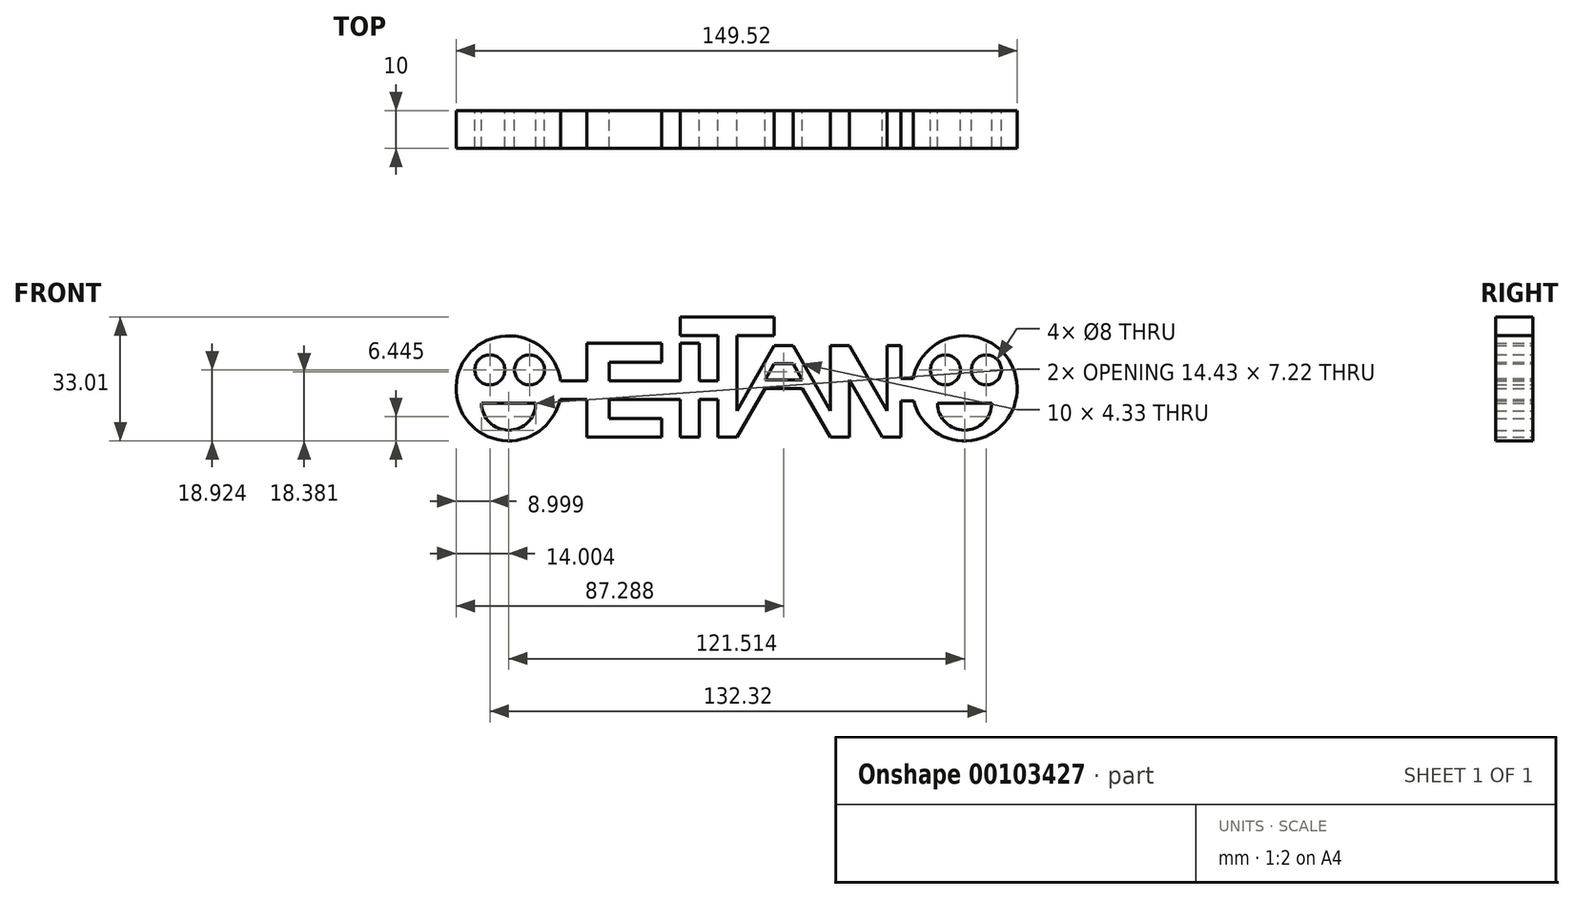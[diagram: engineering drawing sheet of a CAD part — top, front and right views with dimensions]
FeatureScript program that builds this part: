
annotation { "Feature Type Name" : "Feature", "Feature Type Description" : "" }
export const myFeature = defineFeature(function(context is Context, id is Id, definition is map)
    precondition{}
    {
        {
            var Q0;
            Q0=qCreatedBy(makeId("Front.planeOp"),FACE);
            var sketch = newSketch(context, id + "F0", { "sketchPlane" : qUnion([Q0])});
            skLineSegment(sketch, "E0", {"start": v(-39.63, 17.81) * mm, "end": v(-39.63, 22.81) * mm});
            skLineSegment(sketch, "E1", {"start": v(-39.63, 22.81) * mm, "end": v(-59.63, 22.81) * mm});
            skLineSegment(sketch, "E2", {"start": v(-59.63, 22.81) * mm, "end": v(-59.63, 12.81) * mm});
            skLineSegment(sketch, "E3", {"start": v(-39.63, 17.81) * mm, "end": v(-53.56, 17.81) * mm});
            skLineSegment(sketch, "E4", {"start": v(-53.56, 17.81) * mm, "end": v(-53.56, 12.81) * mm});
            skLineSegment(sketch, "E5", {"start": v(-53.56, 12.81) * mm, "end": v(-39.63, 12.81) * mm});
            skLineSegment(sketch, "E6", {"start": v(-59.63, -2.19) * mm, "end": v(-39.63, -2.19) * mm});
            skLineSegment(sketch, "E7", {"start": v(-39.63, -2.19) * mm, "end": v(-39.63, 2.81) * mm});
            skLineSegment(sketch, "E8", {"start": v(-39.63, 2.81) * mm, "end": v(-53.56, 2.81) * mm});
            skLineSegment(sketch, "E9", {"start": v(-53.56, 2.81) * mm, "end": v(-53.56, 7.81) * mm});
            skLineSegment(sketch, "E10", {"start": v(-53.56, 7.81) * mm, "end": v(-39.63, 7.81) * mm});
            skLineSegment(sketch, "E11", {"start": v(-39.63, 12.81) * mm, "end": v(-34.63, 12.81) * mm});
            skLineSegment(sketch, "E12", {"start": v(-39.63, 7.81) * mm, "end": v(-34.63, 7.81) * mm});
            skLineSegment(sketch, "E13", {"start": v(-34.63, 7.81) * mm, "end": v(-34.63, -2.19) * mm});
            skLineSegment(sketch, "E14", {"start": v(-34.63, -2.19) * mm, "end": v(-29.63, -2.19) * mm});
            skLineSegment(sketch, "E15", {"start": v(-29.63, -2.19) * mm, "end": v(-29.63, 7.81) * mm});
            skLineSegment(sketch, "E16", {"start": v(-34.63, 12.81) * mm, "end": v(-34.63, 22.81) * mm});
            skLineSegment(sketch, "E17", {"start": v(-29.63, 22.81) * mm, "end": v(-34.63, 22.81) * mm});
            skLineSegment(sketch, "E18", {"start": v(-29.63, 22.81) * mm, "end": v(-29.63, 12.81) * mm});
            skLineSegment(sketch, "E19.trimOffspring", {"start": v(-29.63, 12.81) * mm, "end": v(-29.63, 22.81) * mm});
            skLineSegment(sketch, "E20", {"start": v(-29.63, 12.81) * mm, "end": v(-24.63, 12.81) * mm});
            skLineSegment(sketch, "E21", {"start": v(-29.63, 7.81) * mm, "end": v(-24.63, 7.81) * mm});
            skLineSegment(sketch, "E22", {"start": v(-24.63, 7.81) * mm, "end": v(-24.63, -2.19) * mm});
            skLineSegment(sketch, "E23", {"start": v(-24.63, -2.19) * mm, "end": v(-19.63, -2.19) * mm});
            skLineSegment(sketch, "E24", {"start": v(-19.63, 4.81) * mm, "end": v(-19.63, 24.81) * mm});
            skLineSegment(sketch, "E25", {"start": v(-24.63, 12.81) * mm, "end": v(-24.63, 24.81) * mm});
            skLineSegment(sketch, "E26", {"start": v(-24.63, 24.81) * mm, "end": v(-34.63, 24.81) * mm});
            skLineSegment(sketch, "E27", {"start": v(-34.63, 24.81) * mm, "end": v(-34.63, 29.81) * mm});
            skLineSegment(sketch, "E28", {"start": v(-19.63, 24.81) * mm, "end": v(-9.63, 24.81) * mm});
            skLineSegment(sketch, "E29", {"start": v(-9.63, 24.81) * mm, "end": v(-9.63, 29.81) * mm});
            skLineSegment(sketch, "E30", {"start": v(-9.63, 29.81) * mm, "end": v(-34.63, 29.81) * mm});
            skLineSegment(sketch, "E31", {"start": v(-19.63, 24.81) * mm, "end": v(-19.63, 4.81) * mm});
            skLineSegment(sketch, "E32", {"start": v(-19.63, 4.81) * mm, "end": v(-9.63, 22.13) * mm});
            skLineSegment(sketch, "E33", {"start": v(-9.63, 22.13) * mm, "end": v(-4.63, 22.13) * mm});
            skLineSegment(sketch, "E34", {"start": v(-4.63, 17.35) * mm, "end": v(-9.63, 17.35) * mm});
            skLineSegment(sketch, "E35", {"start": v(-9.63, 17.35) * mm, "end": v(-12.13, 13.02) * mm});
            skLineSegment(sketch, "E36", {"start": v(-4.63, 22.13) * mm, "end": v(5.37, 4.81) * mm});
            skLineSegment(sketch, "E37", {"start": v(-4.63, 17.35) * mm, "end": v(-2.13, 13.02) * mm});
            skLineSegment(sketch, "E38", {"start": v(-12.13, 13.02) * mm, "end": v(-2.13, 13.02) * mm});
            skLineSegment(sketch, "E39", {"start": v(-19.63, -2.19) * mm, "end": v(-12.13, 10.8) * mm});
            skLineSegment(sketch, "E40", {"start": v(-12.13, 10.8) * mm, "end": v(-2.13, 10.8) * mm});
            skLineSegment(sketch, "E41", {"start": v(-2.13, 10.8) * mm, "end": v(5.37, -2.19) * mm});
            skLineSegment(sketch, "E42", {"start": v(5.37, -2.19) * mm, "end": v(10.37, -2.19) * mm});
            skLineSegment(sketch, "E43", {"start": v(10.37, -2.19) * mm, "end": v(10.37, 13.02) * mm});
            skLineSegment(sketch, "E44", {"start": v(5.37, 4.81) * mm, "end": v(5.37, 22.13) * mm});
            skLineSegment(sketch, "E45", {"start": v(5.37, 22.13) * mm, "end": v(10.37, 22.13) * mm});
            skLineSegment(sketch, "E46", {"start": v(10.37, 13.02) * mm, "end": v(19.15, -2.19) * mm});
            skLineSegment(sketch, "E47", {"start": v(19.15, -2.19) * mm, "end": v(24.15, -2.19) * mm});
            skLineSegment(sketch, "E48", {"start": v(10.37, 22.13) * mm, "end": v(20.37, 4.81) * mm});
            skLineSegment(sketch, "E49", {"start": v(20.37, 4.81) * mm, "end": v(20.37, 22.13) * mm});
            skLineSegment(sketch, "E50", {"start": v(20.37, 22.13) * mm, "end": v(24.15, 22.13) * mm});
            skLineSegment(sketch, "E51", {"start": v(24.15, 22.13) * mm, "end": v(24.15, 13.47) * mm});
            skArc(sketch, "E52", {"start": v(27.52, 7.4) * mm, "mid": v(55.1, 11.17) * mm, "end": v(27.36, 13.47) * mm});
            skPoint(sketch, "E52.centerSnap0", {"position": v(-7.13, 10.8) * mm});
            skPoint(sketch, "E53.endSnap0", {"position": v(15.37, 13.47) * mm});
            skLineSegment(sketch, "E54", {"start": v(24.15, -2.19) * mm, "end": v(24.15, 7.4) * mm});
            skLineSegment(sketch, "E55.trimOffspring", {"start": v(24.15, 7.4) * mm, "end": v(24.15, -2.19) * mm});
            skLineSegment(sketch, "E56", {"start": v(24.15, 13.47) * mm, "end": v(27.36, 13.47) * mm});
            skLineSegment(sketch, "E57", {"start": v(24.15, 7.4) * mm, "end": v(27.52, 7.4) * mm});
            skArc(sketch, "E58", {"start": v(33.88, 6.85) * mm, "mid": v(41.1, -0.36) * mm, "end": v(48.31, 6.85) * mm});
            skLineSegment(sketch, "E59", {"start": v(33.88, 6.85) * mm, "end": v(48.31, 6.85) * mm});
            skCircle(sketch, "E60", {"center": v(35.98, 15.72) * mm, "radius": 4 * mm});
            skCircle(sketch, "E61", {"center": v(46.9, 15.72) * mm, "radius": 4 * mm});
            skLineSegment(sketch, "E62", {"start": v(-59.63, -2.19) * mm, "end": v(-59.63, 7.81) * mm});
            skLineSegment(sketch, "E63.trimOffspring", {"start": v(-59.63, 7.81) * mm, "end": v(-59.63, -2.19) * mm});
            skArc(sketch, "E64", {"start": v(-66.56, 12.81) * mm, "mid": v(-94.4, 11.3) * mm, "end": v(-66.74, 7.81) * mm});
            skLineSegment(sketch, "E65", {"start": v(-59.63, 12.81) * mm, "end": v(-66.56, 12.81) * mm});
            skLineSegment(sketch, "E66", {"start": v(-59.63, 7.81) * mm, "end": v(-66.74, 7.81) * mm});
            skArc(sketch, "E67", {"start": v(-87.63, 6.85) * mm, "mid": v(-80.42, -0.36) * mm, "end": v(-73.2, 6.85) * mm});
            skLineSegment(sketch, "E68", {"start": v(-87.63, 6.85) * mm, "end": v(-73.2, 6.85) * mm});
            skCircle(sketch, "E69", {"center": v(-85.42, 15.72) * mm, "radius": 4 * mm});
            skCircle(sketch, "E70", {"center": v(-74.86, 15.72) * mm, "radius": 4 * mm});
            skLineSegment(sketch, "E71", {"start": v(5.37, 6.9) * mm, "end": v(-3.42, 22.13) * mm});
            skLineSegment(sketch, "E72", {"start": v(-19.63, 6.9) * mm, "end": v(-10.84, 22.13) * mm});
            skLineSegment(sketch, "E73", {"start": v(-10.84, 22.13) * mm, "end": v(-3.42, 22.13) * mm});
            skSolve(sketch);
        }
        {
            var Q0;
            Q0=makeQuery(id+"F0.imprint","IMPRINT",FACE,{"disambiguationData":[TD([[makeQuery(id+"F0.imprint","IMPRINT",EDGE,{"derivedFrom":sQuery(id+"F0.wireOp",EDGE,"E0")}),1.0]])]});
            extrude(context, id + "F1", {"entities" : qUnion([Q0]), "depth" : 10 * mm});
        }
    });
